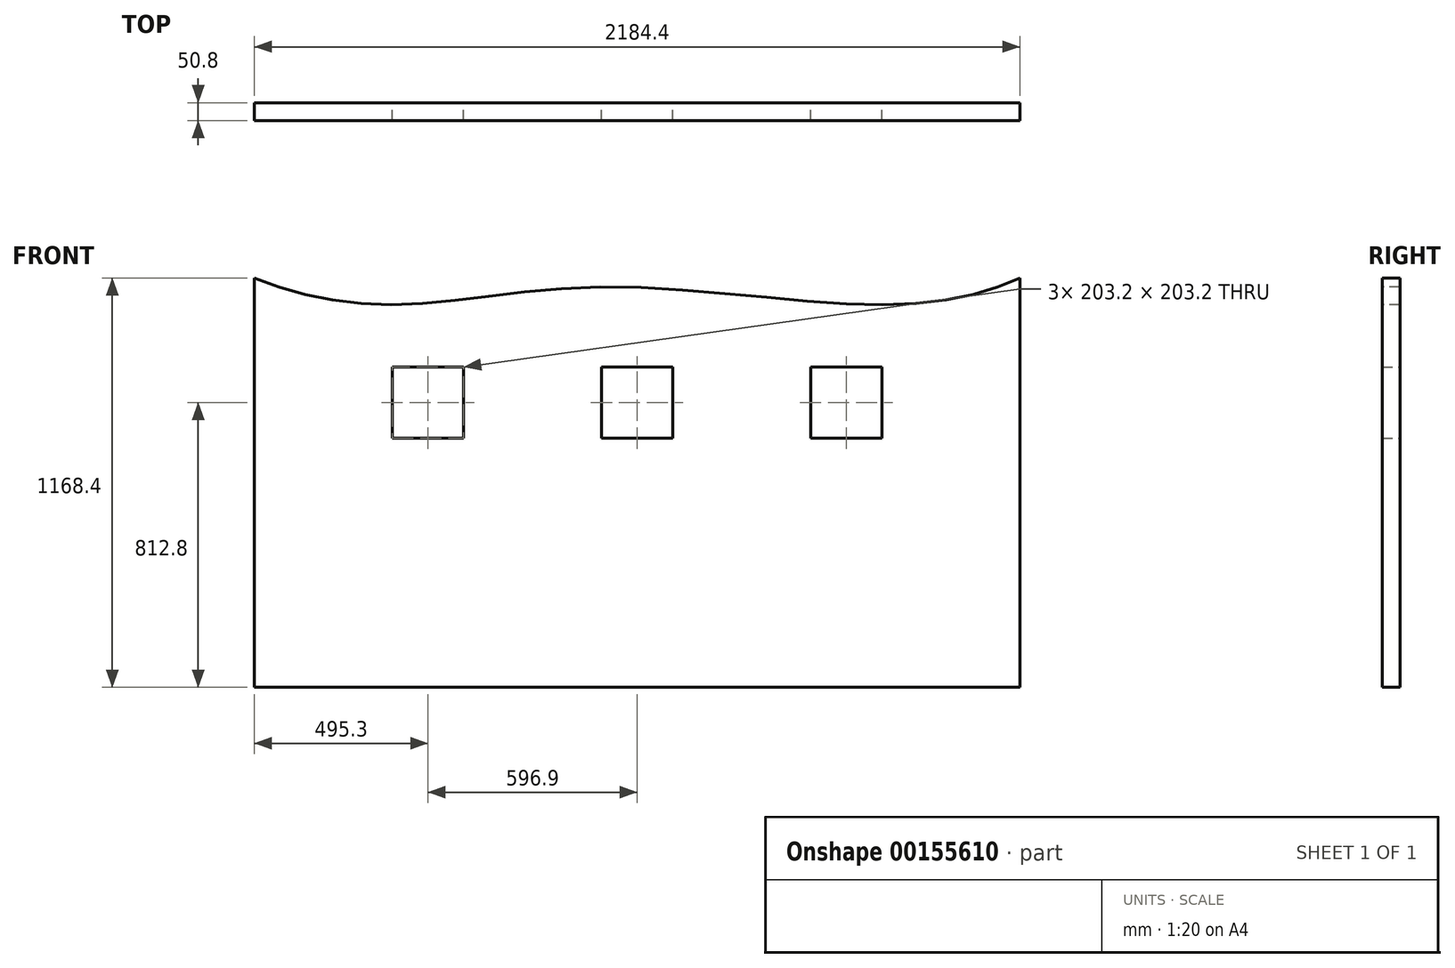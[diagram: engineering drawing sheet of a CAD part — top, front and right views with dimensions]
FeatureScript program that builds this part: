
annotation { "Feature Type Name" : "Feature", "Feature Type Description" : "" }
export const myFeature = defineFeature(function(context is Context, id is Id, definition is map)
    precondition{}
    {
        {
            var Q0;
            Q0=qCreatedBy(makeId("Front.planeOp"),FACE);
            var sketch = newSketch(context, id + "F0", { "sketchPlane" : qUnion([Q0])});
            skLineSegment(sketch, "E0.bottom", {"start": v(-1092.2, 584.2) * mm, "end": v(1092.2, 584.2) * mm});
            skLineSegment(sketch, "E0.top", {"start": v(-1092.2, -584.2) * mm, "end": v(1092.2, -584.2) * mm});
            skLineSegment(sketch, "E0.left", {"start": v(-1092.2, 584.2) * mm, "end": v(-1092.2, -584.2) * mm});
            skLineSegment(sketch, "E0.right", {"start": v(1092.2, 584.2) * mm, "end": v(1092.2, -584.2) * mm});
            skPoint(sketch, "E0.middle", {"position": v(0, 0) * mm});
            skLineSegment(sketch, "E1.bottom", {"start": v(-1092.2, -584.2) * mm, "end": v(-889, -584.2) * mm});
            skLineSegment(sketch, "E1.top", {"start": v(-1092.2, -1092.2) * mm, "end": v(-889, -1092.2) * mm});
            skLineSegment(sketch, "E1.left", {"start": v(-1092.2, -584.2) * mm, "end": v(-1092.2, -1092.2) * mm});
            skLineSegment(sketch, "E1.right", {"start": v(-889, -584.2) * mm, "end": v(-889, -1092.2) * mm});
            skLineSegment(sketch, "E2.bottom", {"start": v(1092.2, -584.2) * mm, "end": v(889, -584.2) * mm});
            skLineSegment(sketch, "E2.top", {"start": v(1092.2, -1092.2) * mm, "end": v(889, -1092.2) * mm});
            skLineSegment(sketch, "E2.left", {"start": v(1092.2, -584.2) * mm, "end": v(1092.2, -1092.2) * mm});
            skLineSegment(sketch, "E2.right", {"start": v(889, -584.2) * mm, "end": v(889, -1092.2) * mm});
            skLineSegment(sketch, "E3.bottom", {"start": v(-495.3, 127) * mm, "end": v(-698.5, 127) * mm});
            skLineSegment(sketch, "E3.top", {"start": v(-495.3, 330.2) * mm, "end": v(-698.5, 330.2) * mm});
            skLineSegment(sketch, "E3.left", {"start": v(-495.3, 127) * mm, "end": v(-495.3, 330.2) * mm});
            skLineSegment(sketch, "E3.right", {"start": v(-698.5, 127) * mm, "end": v(-698.5, 330.2) * mm});
            skPoint(sketch, "E3.middle", {"position": v(-596.9, 228.6) * mm});
            skLineSegment(sketch, "E4.bottom", {"start": v(-101.6, 330.2) * mm, "end": v(101.6, 330.2) * mm});
            skLineSegment(sketch, "E4.top", {"start": v(-101.6, 127) * mm, "end": v(101.6, 127) * mm});
            skLineSegment(sketch, "E4.left", {"start": v(-101.6, 330.2) * mm, "end": v(-101.6, 127) * mm});
            skLineSegment(sketch, "E4.right", {"start": v(101.6, 330.2) * mm, "end": v(101.6, 127) * mm});
            skPoint(sketch, "E4.middle", {"position": v(0, 228.6) * mm});
            skLineSegment(sketch, "E5.bottom", {"start": v(698.5, 330.2) * mm, "end": v(495.3, 330.2) * mm});
            skLineSegment(sketch, "E5.top", {"start": v(698.5, 127) * mm, "end": v(495.3, 127) * mm});
            skLineSegment(sketch, "E5.left", {"start": v(698.5, 330.2) * mm, "end": v(698.5, 127) * mm});
            skLineSegment(sketch, "E5.right", {"start": v(495.3, 330.2) * mm, "end": v(495.3, 127) * mm});
            skPoint(sketch, "E5.middle", {"position": v(596.9, 228.6) * mm});
            skLineSegment(sketch, "E6.bottom", {"start": v(-1016, -736.6) * mm, "end": v(-965.2, -736.6) * mm});
            skLineSegment(sketch, "E6.top", {"start": v(-1016, -889) * mm, "end": v(-965.2, -889) * mm});
            skLineSegment(sketch, "E6.left", {"start": v(-1016, -736.6) * mm, "end": v(-1016, -889) * mm});
            skLineSegment(sketch, "E6.right", {"start": v(-965.2, -736.6) * mm, "end": v(-965.2, -889) * mm});
            skPoint(sketch, "E6.middle", {"position": v(-990.6, -812.8) * mm});
            skLineSegment(sketch, "E7.bottom", {"start": v(965.2, -736.6) * mm, "end": v(1016, -736.6) * mm});
            skLineSegment(sketch, "E7.top", {"start": v(965.2, -889) * mm, "end": v(1016, -889) * mm});
            skLineSegment(sketch, "E7.left", {"start": v(965.2, -736.6) * mm, "end": v(965.2, -889) * mm});
            skLineSegment(sketch, "E7.right", {"start": v(1016, -736.6) * mm, "end": v(1016, -889) * mm});
            skPoint(sketch, "E7.middle", {"position": v(990.6, -812.8) * mm});
            skFitSpline(sketch, "E8", {"points": [v(-1092.2, 584.2) * mm, v(-711.2, 508) * mm, v(-101.6, 558.8) * mm, v(711.2, 508) * mm, v(1092.2, 584.2) * mm], "startDerivative": vector(1569.68, -624.79) * mm, "endDerivative": vector(1366.3, 636.56) * mm});
            skSolve(sketch);
        }
        {
            var Q0;
            Q0=makeQuery(id+"F0.imprint","IMPRINT",FACE,{"disambiguationData":[TD([[makeQuery(id+"F0.imprint","IMPRINT",EDGE,{"derivedFrom":sQuery(id+"F0.wireOp",EDGE,"E1.bottom")}),-1.0]])]});
            var Q1;
            Q1=makeQuery(id+"F0.imprint","IMPRINT",FACE,{"disambiguationData":[TD([[makeQuery(id+"F0.imprint","IMPRINT",EDGE,{"derivedFrom":sQuery(id+"F0.wireOp",EDGE,"E2.bottom")}),1.0]])]});
            var Q2;
            Q2=makeQuery(id+"F0.imprint","IMPRINT",FACE,{"disambiguationData":[TD([[makeQuery(id+"F0.imprint","IMPRINT",EDGE,{"derivedFrom":sQuery(id+"F0.wireOp",EDGE,"E0.top")}),1.0]])]});
            extrude(context, id + "F1", {"entities" : qUnion([Q0, Q1, Q2]), "depth" : 50.8 * mm});
        }
    });
